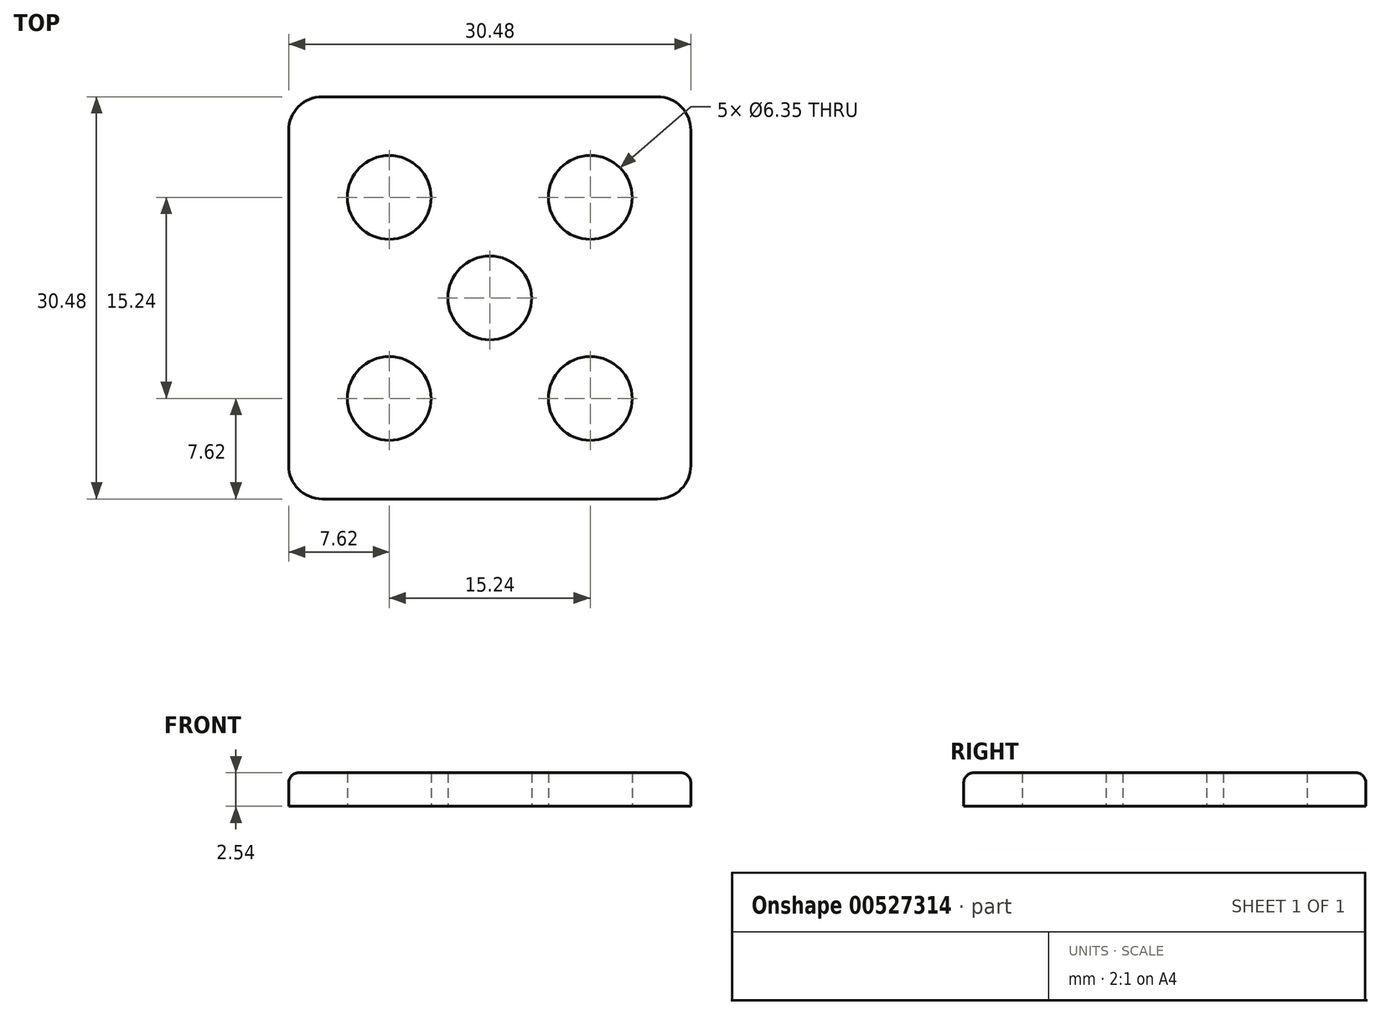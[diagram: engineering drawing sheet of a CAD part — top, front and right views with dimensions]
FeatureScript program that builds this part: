
annotation { "Feature Type Name" : "Feature", "Feature Type Description" : "" }
export const myFeature = defineFeature(function(context is Context, id is Id, definition is map)
    precondition{}
    {
        {
            var Q0;
            Q0=qCreatedBy(makeId("Top.planeOp"),FACE);
            var sketch = newSketch(context, id + "F0", { "sketchPlane" : qUnion([Q0])});
            skLineSegment(sketch, "E0.bottom", {"start": v(2.54, 0) * mm, "end": v(27.94, 0) * mm});
            skLineSegment(sketch, "E0.top", {"start": v(2.54, -30.48) * mm, "end": v(27.94, -30.48) * mm});
            skLineSegment(sketch, "E0.left", {"start": v(0, -2.54) * mm, "end": v(0, -27.94) * mm});
            skLineSegment(sketch, "E0.right", {"start": v(30.48, -2.54) * mm, "end": v(30.48, -27.94) * mm});
            skPoint(sketch, "E1", {"position": v(15.24, -15.24) * mm});
            skCircle(sketch, "E2", {"center": v(15.24, -15.24) * mm, "radius": 3.18 * mm});
            skCircle(sketch, "E3", {"center": v(7.62, -7.62) * mm, "radius": 3.18 * mm});
            skCircle(sketch, "E4", {"center": v(22.86, -7.62) * mm, "radius": 3.18 * mm});
            skCircle(sketch, "E5", {"center": v(22.86, -22.86) * mm, "radius": 3.18 * mm});
            skCircle(sketch, "E6", {"center": v(7.62, -22.86) * mm, "radius": 3.18 * mm});
            skPoint(sketch, "E7.visualSharp", {"position": v(0, 0) * mm});
            skArc(sketch, "E7.filletArc", {"start": v(2.54, 0) * mm, "mid": v(0.74, -0.74) * mm, "end": v(0, -2.54) * mm});
            skPoint(sketch, "E8.visualSharp", {"position": v(30.48, 0) * mm});
            skArc(sketch, "E8.filletArc", {"start": v(30.48, -2.54) * mm, "mid": v(29.74, -0.74) * mm, "end": v(27.94, 0) * mm});
            skPoint(sketch, "E9.visualSharp", {"position": v(30.48, -30.48) * mm});
            skArc(sketch, "E9.filletArc", {"start": v(27.94, -30.48) * mm, "mid": v(29.74, -29.74) * mm, "end": v(30.48, -27.94) * mm});
            skPoint(sketch, "E10.visualSharp", {"position": v(0, -30.48) * mm});
            skArc(sketch, "E10.filletArc", {"start": v(0, -27.94) * mm, "mid": v(0.74, -29.74) * mm, "end": v(2.54, -30.48) * mm});
            skSolve(sketch);
        }
        {
            var Q0;
            Q0 = qSketchRegion(id + "F0", true);
            extrude(context, id + "F1", {"entities" : qUnion([Q0]), "depth" : 2.54 * mm, "offsetDistance" : 25.4 * mm});
        }
        {
            var Q0;
            Q0=makeQuery(id+"F1.opExtrude","CAP_EDGE",EDGE,{"disambiguationData":[OSD([sQuery(id+"F0.wireOp",EDGE,"E0.right")])],"isStart":false});
            fillet(context, id + "F2", {"entities" : qUnion([Q0]), "radius" : 0.76 * mm, "tangentPropagation" : true, "allowEdgeOverflow" : false});
        }
    });
